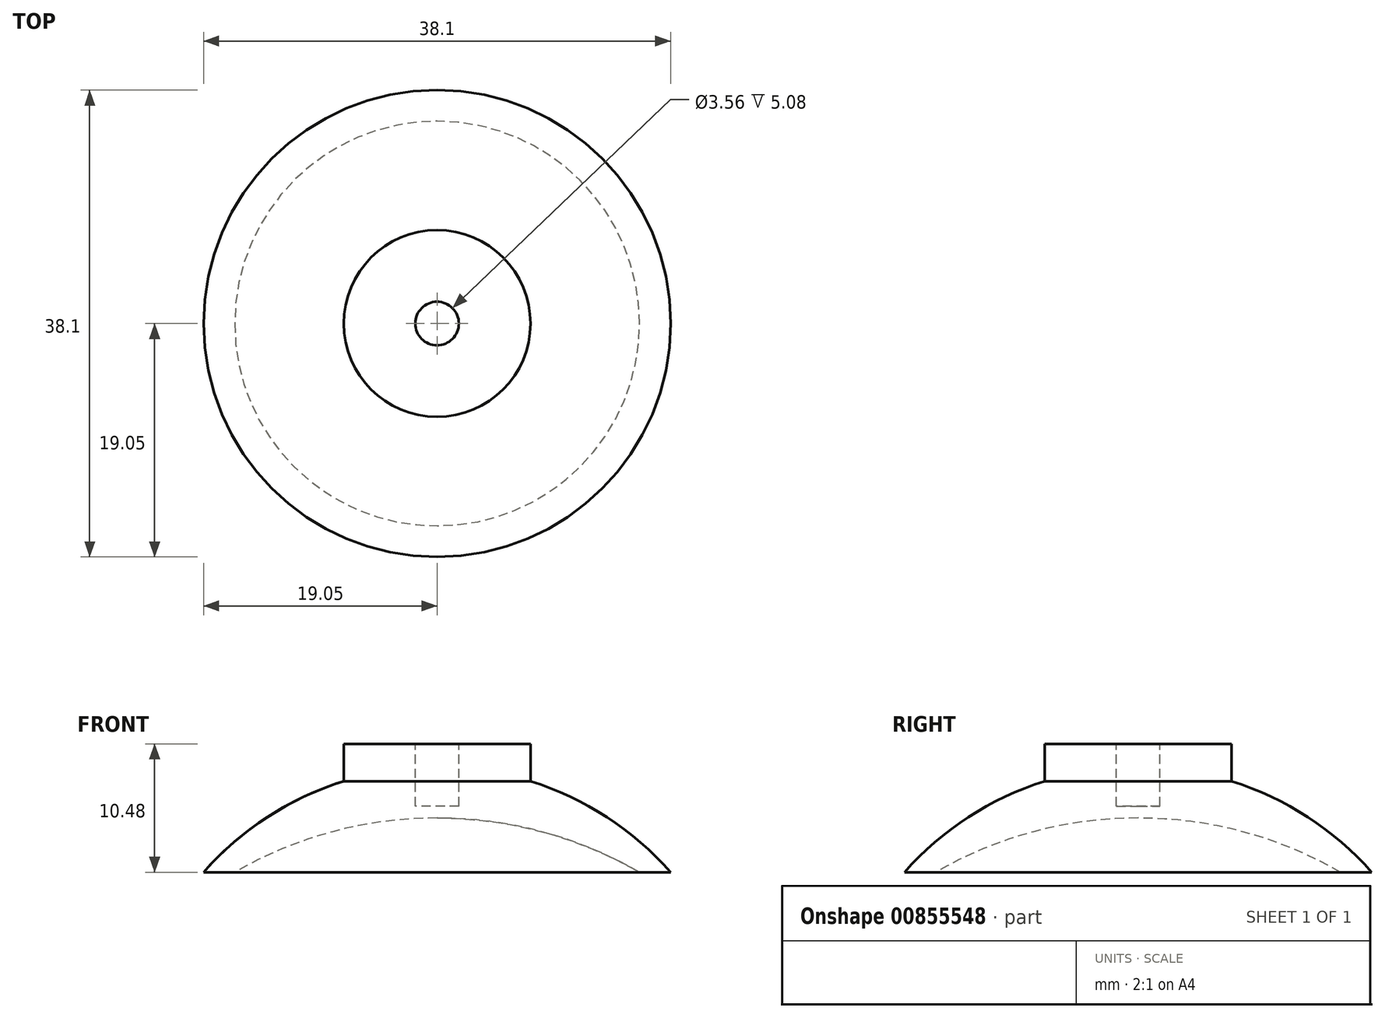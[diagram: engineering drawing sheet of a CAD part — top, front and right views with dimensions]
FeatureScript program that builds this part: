
annotation { "Feature Type Name" : "Feature", "Feature Type Description" : "" }
export const myFeature = defineFeature(function(context is Context, id is Id, definition is map)
    precondition{}
    {
        {
            var Q0;
            Q0=qCreatedBy(makeId("Top.planeOp"),FACE);
            var sketch = newSketch(context, id + "F0", { "sketchPlane" : qUnion([Q0])});
            skArc(sketch, "E0", {"start": v(16.51, 0) * mm, "mid": v(0, 16.51) * mm, "end": v(-16.51, 0) * mm});
            skArc(sketch, "E1", {"start": v(19.05, 0) * mm, "mid": v(0, 19.05) * mm, "end": v(-19.05, 0) * mm});
            skLineSegment(sketch, "E2", {"start": v(-19.05, 0) * mm, "end": v(19.05, 0) * mm});
            skSolve(sketch);
        }
        {
            var Q0;
            Q0=qCreatedBy(makeId("Front.planeOp"),FACE);
            var sketch = newSketch(context, id + "F1", { "sketchPlane" : qUnion([Q0])});
            skArc(sketch, "E3", {"start": v(16.51, 0) * mm, "mid": v(8.55, 3.3) * mm, "end": v(0, 4.42) * mm});
            skArc(sketch, "E4", {"start": v(19.05, 0) * mm, "mid": v(13.84, 4.5) * mm, "end": v(7.62, 7.43) * mm});
            skLineSegment(sketch, "E5", {"start": v(16.51, 0) * mm, "end": v(19.05, 0) * mm});
            skLineSegment(sketch, "E6", {"start": v(0, 8.6) * mm, "end": v(0, 4.42) * mm});
            skLineSegment(sketch, "E7", {"start": v(0, -1.17) * mm, "end": v(0, 6.51) * mm});
            skLineSegment(sketch, "E8.top", {"start": v(0, 10.48) * mm, "end": v(7.62, 10.48) * mm});
            skLineSegment(sketch, "E8.left", {"start": v(0, 6.51) * mm, "end": v(0, 10.48) * mm});
            skLineSegment(sketch, "E8.right", {"start": v(7.62, 7.43) * mm, "end": v(7.62, 10.48) * mm});
            skLineSegment(sketch, "E9.trimOffspring", {"start": v(0, 8.6) * mm, "end": v(0, 19.32) * mm});
            skSolve(sketch);
        }
        {
            var Q0;
            Q0=makeQuery(id+"F1.imprint","IMPRINT",FACE,{"disambiguationData":[TD([[makeQuery(id+"F1.imprint","IMPRINT",EDGE,{"derivedFrom":sQuery(id+"F1.wireOp",EDGE,"E3")}),-1.0]])]});
            var Q1;
            Q1=sQuery(id+"F1.wireOp",EDGE,"E7");
            revolve(context, id + "F2", {"surfaceOperationType" : NewSurfaceOperationType.NEW, "entities" : qUnion([Q0]), "axis" : qUnion([Q1]), "revolveType" : RevolveType.FULL});
        }
        {
            var Q0;
            Q0=makeQuery(id+"F2.opRevolve","SWEPT_FACE",FACE,{"disambiguationData":[OSD([sQuery(id+"F1.wireOp",EDGE,"E8.top")])]});
            var sketch = newSketch(context, id + "F3", { "sketchPlane" : qUnion([Q0])});
            skCircle(sketch, "E10", {"center": v(0, 0) * mm, "radius": 1.78 * mm});
            skSolve(sketch);
        }
        {
            var Q0;
            Q0 = qSketchRegion(id + "F3", true);
            extrude(context, id + "F4", {"entities" : qUnion([Q0]), "operationType" : NewBodyOperationType.REMOVE, "oppositeDirection" : true, "depth" : 5.08 * mm, "offsetDistance" : 25.4 * mm});
        }
    });
